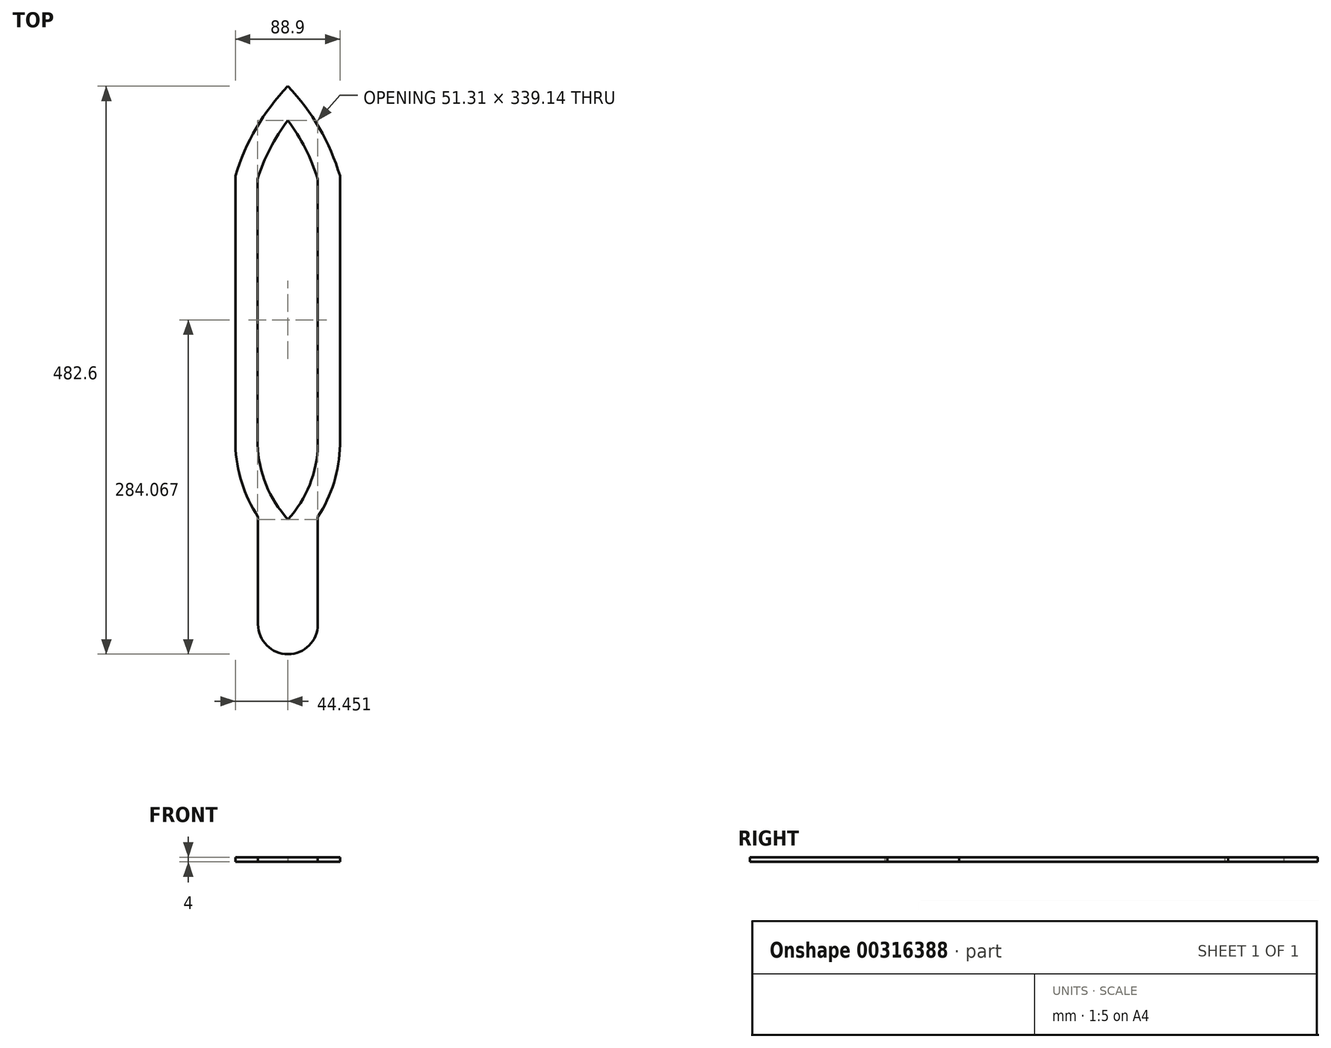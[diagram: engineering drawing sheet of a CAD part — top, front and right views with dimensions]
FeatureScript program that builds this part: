
annotation { "Feature Type Name" : "Feature", "Feature Type Description" : "" }
export const myFeature = defineFeature(function(context is Context, id is Id, definition is map)
    precondition{}
    {
        {
            var Q0;
            Q0=qCreatedBy(makeId("Top.planeOp"),FACE);
            var sketch = newSketch(context, id + "F0", { "sketchPlane" : qUnion([Q0])});
            skLineSegment(sketch, "E0.bottom", {"start": v(25.4, -88.9) * mm, "end": v(-25.4, -88.9) * mm});
            skLineSegment(sketch, "E0.top", {"start": v(25.4, 88.9) * mm, "end": v(-25.4, 88.9) * mm});
            skLineSegment(sketch, "E0.left", {"start": v(25.4, -88.9) * mm, "end": v(25.4, 88.9) * mm});
            skLineSegment(sketch, "E0.right", {"start": v(-25.4, -88.9) * mm, "end": v(-25.4, 88.9) * mm});
            skPoint(sketch, "E0.middle", {"position": v(0, 0) * mm});
            skLineSegment(sketch, "E1", {"start": v(0, 88.9) * mm, "end": v(93.28, 88.9) * mm, "construction": true});
            skLineSegment(sketch, "E2", {"start": v(0, 88.9) * mm, "end": v(-88.42, 88.9) * mm, "construction": true});
            skPoint(sketch, "E3", {"position": v(-44.72, 88.9) * mm});
            skPoint(sketch, "E4", {"position": v(44.18, 88.9) * mm});
            skLineSegment(sketch, "E5", {"start": v(-44.72, 88.9) * mm, "end": v(-44.72, 317.5) * mm});
            skLineSegment(sketch, "E6", {"start": v(44.18, 88.9) * mm, "end": v(44.18, 317.5) * mm});
            skLineSegment(sketch, "E7", {"start": v(0, 317.5) * mm, "end": v(0, 393.7) * mm, "construction": true});
            skArc(sketch, "E8", {"start": v(0, 393.7) * mm, "mid": v(-26.94, 358.29) * mm, "end": v(-44.72, 317.5) * mm});
            skArc(sketch, "E9", {"start": v(44.18, 317.5) * mm, "mid": v(26.65, 358.25) * mm, "end": v(0, 393.7) * mm});
            skPoint(sketch, "E10", {"position": v(0, 27.78) * mm});
            skArc(sketch, "E11", {"start": v(-44.72, 88.9) * mm, "mid": v(-32.17, 39.51) * mm, "end": v(0, 0) * mm});
            skLineSegment(sketch, "E12", {"start": v(0, 27.78) * mm, "end": v(-25.4, 27.78) * mm, "construction": true});
            skLineSegment(sketch, "E13", {"start": v(0, 27.78) * mm, "end": v(25.4, 27.78) * mm, "construction": true});
            skArc(sketch, "E14", {"start": v(0, 0) * mm, "mid": v(32.09, 39.48) * mm, "end": v(44.18, 88.9) * mm});
            skArc(sketch, "E15.0", {"start": v(25.39, 314.71) * mm, "mid": v(14.76, 340.8) * mm, "end": v(-0.09, 364.73) * mm});
            skLineSegment(sketch, "E15.1", {"start": v(-25.92, 89.2) * mm, "end": v(-25.92, 314.67) * mm});
            skArc(sketch, "E15.2", {"start": v(-25.92, 89.2) * mm, "mid": v(-18.62, 55.1) * mm, "end": v(0.02, 25.6) * mm});
            skArc(sketch, "E15.3", {"start": v(-0.09, 364.73) * mm, "mid": v(-15.12, 340.8) * mm, "end": v(-25.92, 314.67) * mm});
            skArc(sketch, "E15.4", {"start": v(0.02, 25.6) * mm, "mid": v(18.47, 55.04) * mm, "end": v(25.39, 89.08) * mm});
            skLineSegment(sketch, "E15.5", {"start": v(25.39, 89.08) * mm, "end": v(25.39, 314.71) * mm});
            skSolve(sketch);
        }
        {
            var Q0;
            {var subQ2=sQuery(id+"F0.wireOp",EDGE,"E5");Q0=makeQuery(id+"F0.imprint","IMPRINT",FACE,{"disambiguationData":[TD([[makeQuery(id+"F0.imprint","IMPRINT",EDGE,{"derivedFrom":subQ2}),-1.0]])]});}
            var Q1;
            {var subQ6=sQuery(id+"F0.wireOp",EDGE,"E0.bottom");Q1=makeQuery(id+"F0.imprint","IMPRINT",FACE,{"disambiguationData":[TD([[makeQuery(id+"F0.imprint","IMPRINT",EDGE,{"derivedFrom":subQ6}),-1.0]])]});}
            var Q2;
            {var subQ5=sQuery(id+"F0.wireOp",EDGE,"E0.left");var subQ6=sQuery(id+"F0.wireOp",EDGE,"E0.top");var subQ7=makeQuery(id+"F0.imprint","INTERSECT",VERTEX,{"derivedFrom":[subQ6,subQ5]});Q2=makeQuery(id+"F0.imprint","IMPRINT",FACE,{"disambiguationData":[TD([[makeQuery(id+"F0.imprint","IMPRINT",EDGE,{"disambiguationData":[TD([[subQ7,-1.0]])],"derivedFrom":subQ6}),1.0]])]});}
            extrude(context, id + "F1", {"entities" : qUnion([Q0, Q1, Q2]), "depth" : 4 * mm});
        }
        {
            var Q0;
            Q0=makeQuery(id+"F1.opExtrude","SWEPT_EDGE",EDGE,{"disambiguationData":[OSD([sQuery(id+"F0.wireOp",EDGE,"E0.bottom"),sQuery(id+"F0.wireOp",EDGE,"E0.right")])]});
            var Q1;
            Q1=makeQuery(id+"F1.opExtrude","SWEPT_EDGE",EDGE,{"disambiguationData":[OSD([sQuery(id+"F0.wireOp",EDGE,"E0.bottom"),sQuery(id+"F0.wireOp",EDGE,"E0.left")])]});
            fillet(context, id + "F2", {"entities" : qUnion([Q0, Q1]), "radius" : 25.4 * mm, "tangentPropagation" : true, "allowEdgeOverflow" : false});
        }
    });
